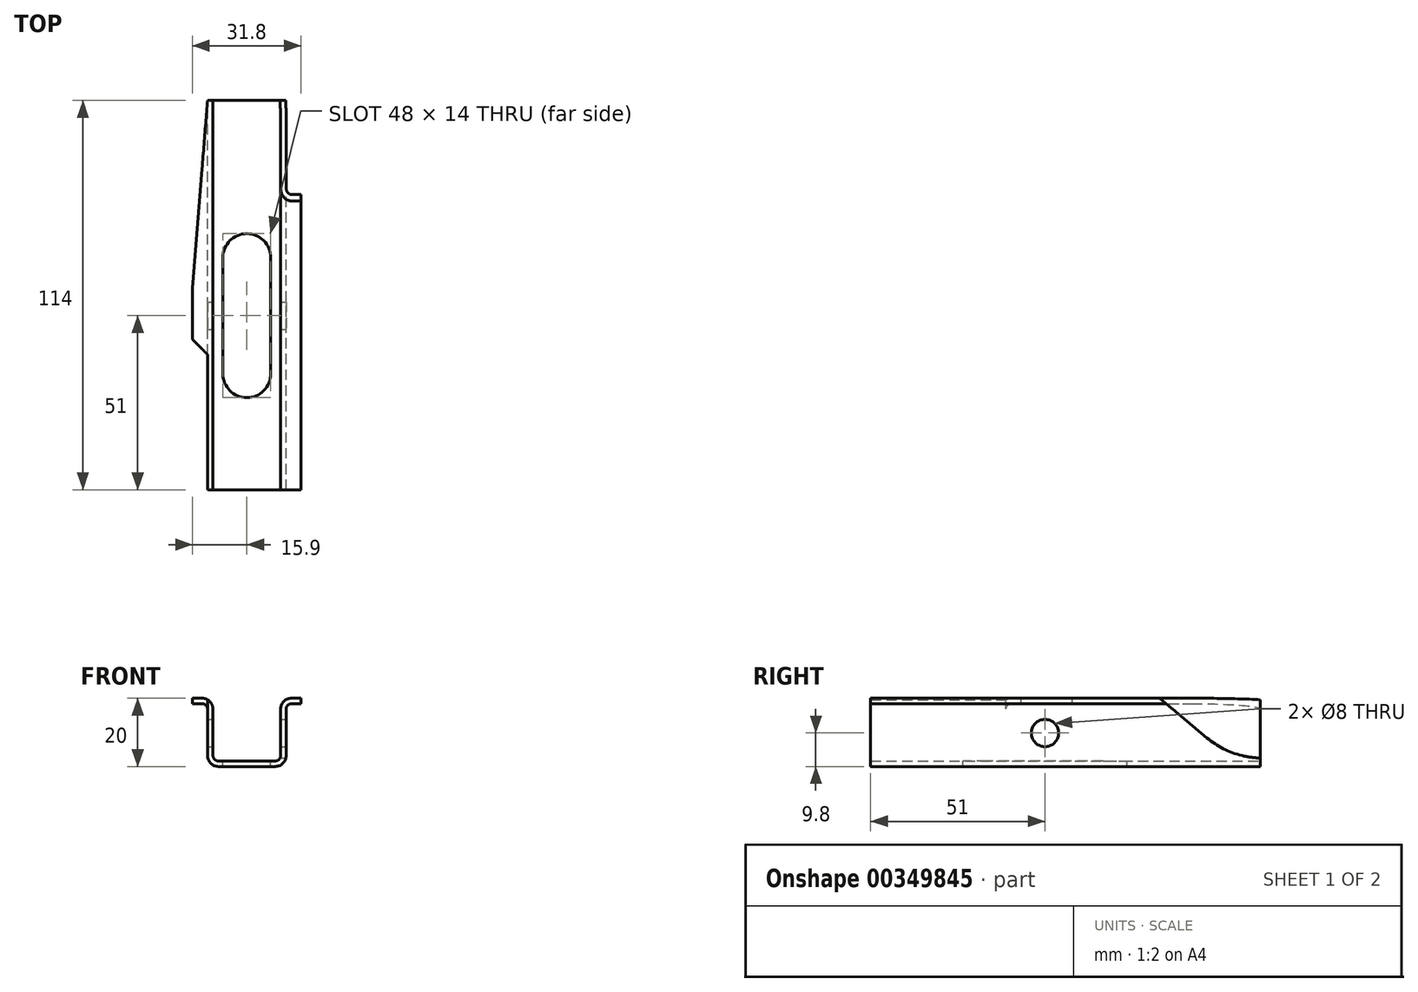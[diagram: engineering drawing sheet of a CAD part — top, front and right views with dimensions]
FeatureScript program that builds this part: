
annotation { "Feature Type Name" : "Feature", "Feature Type Description" : "" }
export const myFeature = defineFeature(function(context is Context, id is Id, definition is map)
    precondition{}
    {
        {
            var Q0;
            Q0=qCreatedBy(makeId("Front.planeOp"),FACE);
            var sketch = newSketch(context, id + "F0", { "sketchPlane" : qUnion([Q0])});
            skLineSegment(sketch, "E0", {"start": v(-8.3, 0) * mm, "end": v(0, 0) * mm});
            skLineSegment(sketch, "E1", {"start": v(-8.3, 1.6) * mm, "end": v(0, 1.6) * mm});
            skLineSegment(sketch, "E2", {"start": v(-11.5, 3.2) * mm, "end": v(-11.5, 16.8) * mm});
            skLineSegment(sketch, "E3", {"start": v(-9.9, 3.2) * mm, "end": v(-9.9, 16.8) * mm});
            skLineSegment(sketch, "E4", {"start": v(-13.1, 20) * mm, "end": v(-15.9, 20) * mm});
            skLineSegment(sketch, "E5", {"start": v(-15.9, 20) * mm, "end": v(-15.9, 18.4) * mm});
            skPoint(sketch, "E6.endSnap0", {"position": v(-15.9, 18.08) * mm});
            skPoint(sketch, "E7.orphan", {"position": v(-26.3, 18.08) * mm});
            skPoint(sketch, "E8.orphan", {"position": v(-15.9, 16.17) * mm});
            skLineSegment(sketch, "E9", {"start": v(-13.1, 18.4) * mm, "end": v(-15.9, 18.4) * mm});
            skPoint(sketch, "E10.visualSharp", {"position": v(-11.5, 18.4) * mm});
            skArc(sketch, "E10.filletArc", {"start": v(-11.5, 16.8) * mm, "mid": v(-11.97, 17.93) * mm, "end": v(-13.1, 18.4) * mm});
            skPoint(sketch, "E11.visualSharp", {"position": v(-9.9, 1.6) * mm});
            skArc(sketch, "E11.filletArc", {"start": v(-9.9, 3.2) * mm, "mid": v(-9.43, 2.07) * mm, "end": v(-8.3, 1.6) * mm});
            skPoint(sketch, "E12.visualSharp", {"position": v(-9.9, 20) * mm});
            skArc(sketch, "E12.filletArc", {"start": v(-9.9, 16.8) * mm, "mid": v(-10.84, 19.06) * mm, "end": v(-13.1, 20) * mm});
            skPoint(sketch, "E13.visualSharp", {"position": v(-11.5, 0) * mm});
            skArc(sketch, "E13.filletArc", {"start": v(-11.5, 3.2) * mm, "mid": v(-10.56, 0.94) * mm, "end": v(-8.3, 0) * mm});
            skLineSegment(sketch, "E14", {"start": v(0, 0) * mm, "end": v(0, 25.46) * mm, "construction": true});
            skLineSegment(sketch, "E15.MirrorCS", {"start": v(15.9, 20) * mm, "end": v(15.9, 18.4) * mm});
            skPoint(sketch, "E16.MirrorP", {"position": v(26.3, 18.08) * mm});
            skArc(sketch, "E17.MirrorCS", {"start": v(9.9, 3.2) * mm, "mid": v(9.43, 2.07) * mm, "end": v(8.3, 1.6) * mm});
            skArc(sketch, "E18.MirrorCS", {"start": v(11.5, 16.8) * mm, "mid": v(11.97, 17.93) * mm, "end": v(13.1, 18.4) * mm});
            skLineSegment(sketch, "E19.MirrorCS", {"start": v(8.3, 0) * mm, "end": v(0, 0) * mm});
            skLineSegment(sketch, "E20.MirrorCS", {"start": v(8.3, 1.6) * mm, "end": v(0, 1.6) * mm});
            skPoint(sketch, "E21.MirrorP", {"position": v(9.9, 1.6) * mm});
            skLineSegment(sketch, "E22.MirrorCS", {"start": v(11.5, 3.2) * mm, "end": v(11.5, 16.8) * mm});
            skLineSegment(sketch, "E23.MirrorCS", {"start": v(9.9, 3.2) * mm, "end": v(9.9, 16.8) * mm});
            skPoint(sketch, "E24.MirrorP", {"position": v(15.9, 18.08) * mm});
            skPoint(sketch, "E25.MirrorP", {"position": v(15.9, 16.17) * mm});
            skPoint(sketch, "E26.MirrorP", {"position": v(11.5, 18.4) * mm});
            skArc(sketch, "E27.MirrorCS", {"start": v(11.5, 3.2) * mm, "mid": v(10.56, 0.94) * mm, "end": v(8.3, 0) * mm});
            skLineSegment(sketch, "E28.MirrorCS", {"start": v(13.1, 18.4) * mm, "end": v(15.9, 18.4) * mm});
            skArc(sketch, "E29.MirrorCS", {"start": v(9.9, 16.8) * mm, "mid": v(10.84, 19.06) * mm, "end": v(13.1, 20) * mm});
            skPoint(sketch, "E30.MirrorP", {"position": v(9.9, 20) * mm});
            skPoint(sketch, "E31.MirrorP", {"position": v(11.5, 0) * mm});
            skLineSegment(sketch, "E32.MirrorCS", {"start": v(13.1, 20) * mm, "end": v(15.9, 20) * mm});
            skSolve(sketch);
        }
        {
            var Q0;
            Q0 = qSketchRegion(id + "F0", true);
            extrude(context, id + "F1", {"entities" : qUnion([Q0]), "depth" : 114 * mm});
        }
        {
            var Q0;
            Q0=makeQuery(id+"F1.opExtrude","SWEPT_FACE",FACE,{"disambiguationData":[OSD([sQuery(id+"F0.wireOp",EDGE,"E1"),sQuery(id+"F0.wireOp",EDGE,"E20.MirrorCS")])]});
            var sketch = newSketch(context, id + "F2", { "sketchPlane" : qUnion([Q0])});
            skLineSegment(sketch, "E33.bottom", {"start": v(7, -46) * mm, "end": v(-7, -46) * mm});
            skLineSegment(sketch, "E33.top", {"start": v(7, -80) * mm, "end": v(-7, -80) * mm});
            skLineSegment(sketch, "E33.left", {"start": v(7, -46) * mm, "end": v(7, -80) * mm});
            skLineSegment(sketch, "E33.right", {"start": v(-7, -46) * mm, "end": v(-7, -80) * mm});
            skPoint(sketch, "E33.middle", {"position": v(0, -63) * mm});
            skLineSegment(sketch, "E34", {"start": v(0, 0) * mm, "end": v(0, -144.93) * mm, "construction": true});
            skCircle(sketch, "E35", {"center": v(0, -46) * mm, "radius": 7 * mm});
            skCircle(sketch, "E36", {"center": v(0, -80) * mm, "radius": 7 * mm});
            skSolve(sketch);
        }
        {
            var Q0;
            Q0 = qSketchRegion(id + "F2", true);
            extrude(context, id + "F3", {"entities" : qUnion([Q0]), "operationType" : NewBodyOperationType.REMOVE, "oppositeDirection" : true, "depth" : 25 * mm});
        }
        {
            var Q0;
            Q0=makeQuery(id+"F1.opExtrude","SWEPT_FACE",FACE,{"disambiguationData":[OSD([sQuery(id+"F0.wireOp",EDGE,"E4")])]});
            var sketch = newSketch(context, id + "F4", { "sketchPlane" : qUnion([Q0])});
            skLineSegment(sketch, "E37", {"start": v(-15.9, 0) * mm, "end": v(-11.5, 0) * mm});
            skPoint(sketch, "E37.endSnap0", {"position": v(-14.5, 0) * mm});
            skLineSegment(sketch, "E38", {"start": v(-11.5, 0) * mm, "end": v(-15.9, -55) * mm});
            skLineSegment(sketch, "E39", {"start": v(-15.9, -55) * mm, "end": v(-15.9, 0) * mm});
            skLineSegment(sketch, "E40", {"start": v(-15.9, -70) * mm, "end": v(-11.5, -74.4) * mm});
            skLineSegment(sketch, "E41", {"start": v(-11.5, -74.4) * mm, "end": v(-11.5, -114) * mm});
            skLineSegment(sketch, "E42", {"start": v(-11.5, -114) * mm, "end": v(-15.9, -114) * mm});
            skLineSegment(sketch, "E43", {"start": v(-15.9, -114) * mm, "end": v(-15.9, -70) * mm});
            skSolve(sketch);
        }
        {
            var Q0;
            Q0 = qSketchRegion(id + "F4", true);
            extrude(context, id + "F5", {"entities" : qUnion([Q0]), "operationType" : NewBodyOperationType.REMOVE, "oppositeDirection" : true, "depth" : 5 * mm});
        }
        {
            var Q0;
            Q0=makeQuery(id+"F1.opExtrude","SWEPT_FACE",FACE,{"disambiguationData":[OSD([sQuery(id+"F0.wireOp",EDGE,"E22.MirrorCS")])]});
            var sketch = newSketch(context, id + "F6", { "sketchPlane" : qUnion([Q0])});
            skCircle(sketch, "E44", {"center": v(-63, 9.8) * mm, "radius": 4 * mm});
            skSolve(sketch);
        }
        {
            var Q0;
            Q0 = qSketchRegion(id + "F6", true);
            extrude(context, id + "F7", {"entities" : qUnion([Q0]), "operationType" : NewBodyOperationType.REMOVE, "oppositeDirection" : true, "depth" : 30 * mm});
        }
        {
            var Q0;
            Q0=makeQuery(id+"F1.opExtrude","SWEPT_FACE",FACE,{"disambiguationData":[OSD([sQuery(id+"F0.wireOp",EDGE,"E22.MirrorCS")])]});
            var sketch = newSketch(context, id + "F8", { "sketchPlane" : qUnion([Q0])});
            skArc(sketch, "E45", {"start": v(-15.57, 8.35) * mm, "mid": v(-8.05, 4) * mm, "end": v(0.5, 2.5) * mm});
            skLineSegment(sketch, "E46", {"start": v(-15.57, 8.35) * mm, "end": v(-38.4, 27.5) * mm});
            skLineSegment(sketch, "E47", {"start": v(0.5, 2.5) * mm, "end": v(5, 2.5) * mm});
            skLineSegment(sketch, "E48", {"start": v(5, 2.5) * mm, "end": v(5, 27.5) * mm});
            skLineSegment(sketch, "E49", {"start": v(-38.4, 27.5) * mm, "end": v(5, 27.5) * mm});
            skSolve(sketch);
        }
        {
            var Q0;
            Q0 = qSketchRegion(id + "F8", true);
            extrude(context, id + "F9", {"entities" : qUnion([Q0]), "operationType" : NewBodyOperationType.REMOVE, "endBound" : BoundingType.SYMMETRIC, "oppositeDirection" : true, "depth" : 10 * mm});
        }
    });
